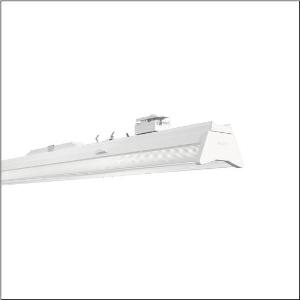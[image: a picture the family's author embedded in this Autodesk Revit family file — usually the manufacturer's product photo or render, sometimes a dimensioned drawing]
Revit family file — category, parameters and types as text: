
# Revit family: licross_r__21_performance_ho_52td16cn4c5m_c92a
name_source: partatom
category: Lighting Fixtures
units: mm (PartAtom-declared; Revit-internal decimal feet)

## family parameters
Cut with Voids When Loaded = No
Host = Face
Light Source = No
Part Type = Normal
Room Calculation Point = No
Round Connector Dimension = Use Diameter
Shared = No

## types (1)
- --- (1 x LED, 12610 lm, 68.9 W, 4000K)
    Apparent Load = 69 VA
    CIE Flux Codes = 63 87 95 78 100
    Color Rendering = 80
    Color Temperature = 4000K
    Default Elevation = 1800 mm
    Description = Licross® 21 Performance HO, luminaire insert, of sheet steel, galvanised, coil coated, white, length: 1.500mm, width: 120mm, height: 123mm, LED rated luminous flux: 12.610lm, light colour: 840, control gear: ON/OFF Multilumen, CLOi, control gear: ECG Multilumen, with plug, 3-pole, with phase selection, mains connection: 220..240V, AC, 50/60Hz, start of lifetime: 69W, end of service life: 83W, halogen-free wiring, primary light control with lens, of plastic, primary optical cover: cover, of PMMA, light emission: direct/indirect distribution, primary light characteristic: symmetric, protection rating (complete): IP54, insulation class (complete): insulation class I (protective earthing), certification: CE, ENEC, UKCA, protection symbol: D if used in an environment with non-conductive dust loads with corresponding accessories, impact resistance: IK06, permissible ambient temperature for indoor applications: -35..+35°C, corresponds to IFS (International Featured Standards) requirements for safety and quality in the food industry, reducing of maximum allowable ambient temperature of 5°C with ceiling mounting, LABS conformity tested according to VDMA 24364:2018-05, packaging unit: 1 piece
    Height = 114 mm
    Lamp = 1 x LED
    Lamp Light Flux = 12610 lm
    Lamp Power = 68.9 W
    Lamp count = 1
    Length = 1500 mm
    Luminous efficacy = 183 lm/W
    Manufacturer = Siteco
    ModVariant = No
    Model = 52TD16CN4C5M
    Mounting Place = Ceiling
    Mounting Type = Pendant
    Number of Poles = 1
    OnlyDefault = Yes
    Power Factor = 1
    Product Name = Licross® 21 Performance HO
    Product group = luminaire insert
    ProductGroupID = 901
    Protection Class = Protection class I
    Protection Degree = IP 54
    RLX_Detail_Level = 1
    RLX_Emergency_Light_Flux = 0 lm
    RLX_Emergency_Type = 0
    RLX_Emergency_Type_DB = No
    RlxData = <blob elided: 31917 chars, md5=3f120709>
    Socket = socket
    Standby Power = 0 W
    System Light Flux = 12610 lm
    System Power = 69 W
    Type Comments = factory setting: luminous flux: 100 % | (A | C | E) | 162 mA
    Type Image = l_1256138.jpg
    URL = http://relux.com
    VarID = @adj_080461
    Voltage = 0 V
    Weight = 0.00 kg
    Width = 120 mm

## geometry (parser evidence)
native form markers: Blend x4, Sweep x12
no freeform markers — native parametric forms only
